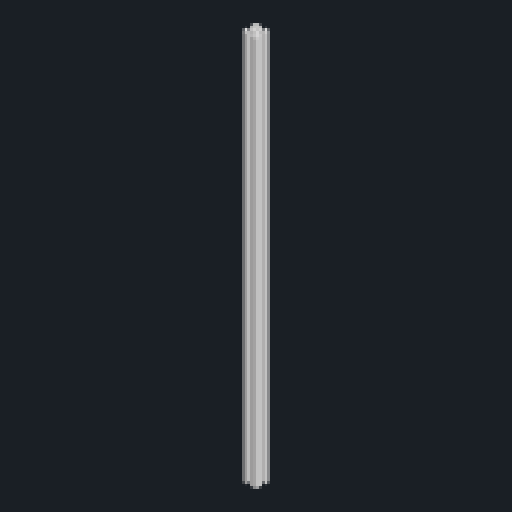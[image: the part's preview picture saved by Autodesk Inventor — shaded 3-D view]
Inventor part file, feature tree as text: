
AUTODESK INVENTOR PART (.ipt)
format: ipt  version: 2023.1 (Build 271208000, 208)  size: 141,312 bytes
history: native  units: mm
features: extrude x2, sketch x1, pattern_circular x1, fillet x1
ambient origin geometry x8: Origin, YZ Plane, XZ Plane, XY Plane, X Axis, Y Axis, Z Axis, Center Point
bodies: Solid1 (feature_tree)
feature tree (5):
  sketch  "Sketch1"  dims[d0=4.3mm d1=20.0mm d2=20.0mm d3=5.0mm d4=6.4mm d5=560.0mm d6=0.0mm d7=560.0mm d8=0.0mm d9=40.0mm d10=360.0deg d14=11.5mm d15=2.0mm]
  extrude  "Extrusion1"  Depth=20.0mm
  extrude  "Extrusion2"  Depth=20.0mm
  pattern_circular  "Circular Pattern1"  [2 undecoded]
  fillet  "Fillet1"  Radius=6.4mm
note: 2 required parameter values undecoded (feature->parameter linkage not recoverable at this tier; creation-order binding heuristic only, values carry confidence <= 0.55)
